# Revit family: PRD_FrankeWS_WlHngWshBsns_AnimaTrapCover_BS206
name_source: partatom
category: Furniture
revit_build: Autodesk Revit 2018 (Build: 20190510_1515(x64)
units: mm (PartAtom-declared; Revit-internal decimal feet)

## family parameters
Cut with Voids When Loaded = No
Host = Face
OmniClass Number = 23.40.20.21
OmniClass Title = Toilet and Bath Specialties
Room Calculation Point = No
Shared = No

## types (1)
- PRD_FrankeWS_WlHngWshBsns_AnimaTrapCover_BS206
    AssetType = Fixed
    BIMObjectName = PRD_AR_WallHungWashBasins_AnimaTrapCover_BS206
    Category = Pr_40_20_96_96, Wall-hung wash basins
    Color = Stainless steel
    Default Elevation = 820 mm
    Description = Wall mounted trap cover for wash basin BS204 and BS205, stainless steel, surface high polished, material thickness 1 mm, not closed at bottom, incl. screws and dowels.
    DurationUnit = year
    Features = stainless steel, 1.00 mm, satin finished, wall mounting, 542x410x244 mm (WxHxD)
    Finish = Satin finished
    GrossWeight = 4.70 kg
    IfcExportAs = IfcFurnitureType
    IfcExportType = NOTDEFINED
    MainColor = Stainless steel
    Manufacturer = KWC Group AG
    ManufacturerName = KWC Group AG
    ManufacturerURL = www.kwc.com
    Material = Stainless steel 1.4301
    Model = BS206
    ModelNumber = 2000058442
    ModelReference = BS206
    NBSDescription = Wall hung wash basins
    NBSReference = 45-35-70/369
    Name = ANIMA trap cover BS206
    NetWeight = 4.70 kg
    NominalDepth = 244 mm
    NominalHeight = 410 mm  [stored 1.34514 ft]
    NominalLength = 542 mm
    NominalWidth = 0 mm  [stored 0 ft]
    ProductInformation = https://pim.kwc.com
    Size = 542 x 410 x 244 mm
    Style = Trap cover
    TrapCoverMaterial = PRD_AR_StainlessSteel_SatinFinished
    URL = www.kwc.com
    Uniclass2015Code = Pr_40_20_96_96
    Uniclass2015Title = Wall-hung wash basins
    Uniclass2015Version = Products v1.5
    Version = 1
    WarrantyDurationUnit = year

note: [stored X ft] marks values corroborated as IEEE doubles in the binary element streams (Revit-internal decimal feet)

## geometry (parser evidence)
native form markers: Sweep x2
no freeform markers — native parametric forms only
